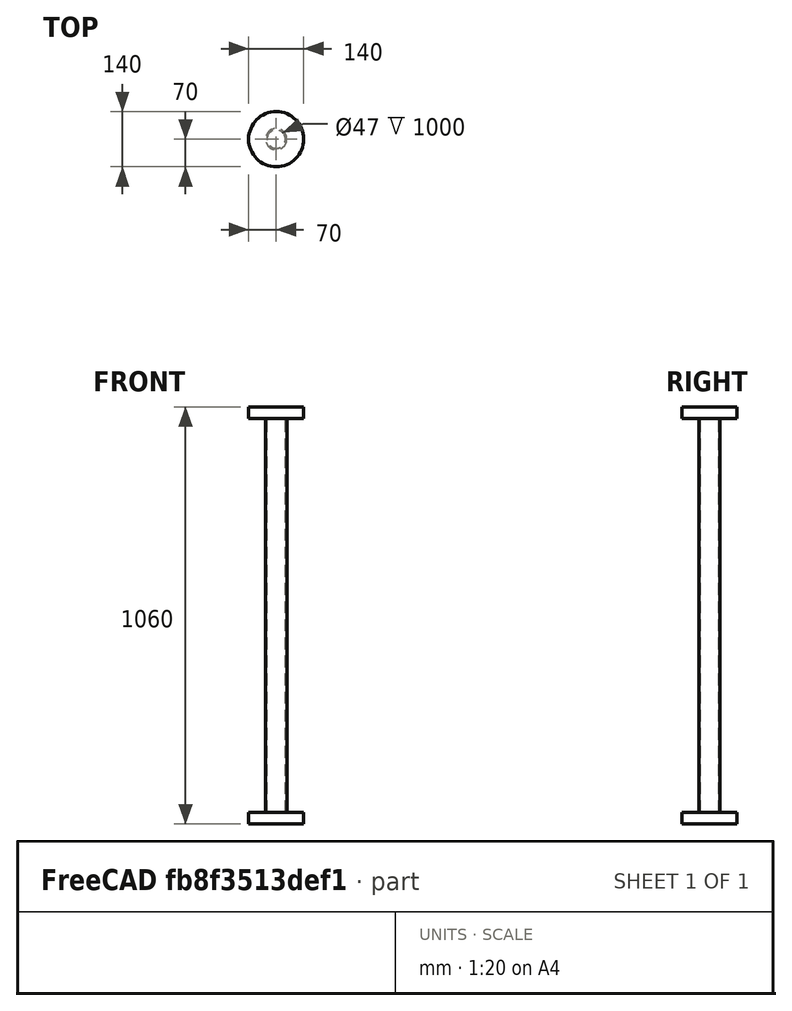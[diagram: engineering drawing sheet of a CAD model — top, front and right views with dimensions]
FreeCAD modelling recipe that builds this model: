
FCSTD DOCUMENT  (FreeCAD 0.19R)
Label: model
License: All rights reserved
LicenseURL: http://en.wikipedia.org/wiki/All_rights_reserved
objects: Mesh::Feature×3, Part::Cylinder×2, Part::FeaturePython×1
note: 3 computed .brp shape members not serialized (recipe doc carries the construction recipe); baked Part::Feature solids carry a one-line shape summary decoded from their .brp

FEATURE [Part::FeaturePython] Tube  # WARN: FeaturePython — macro-defined, semantics opaque (R4)
  AttacherType = Attacher::AttachEngine3D
  Height = 1000
  InnerRadius = 23.5
  OuterRadius = 27
FEATURE [Part::Cylinder] Cylinder001
  Angle = 360
  AttacherType = Attacher::AttachEngine3D
  Height = 30
  Placement = pos=(0,0,-30) rot=(0,0,1;0rad)
  Radius = 70
FEATURE [Part::Cylinder] Cylinder003
  Angle = 360
  AttacherType = Attacher::AttachEngine3D
  Height = 30
  Placement = pos=(0,0,1000) rot=(0,0,1;0rad)
  Radius = 70
FEATURE [Mesh::Feature] Mesh001  label="Cylinder001 (Meshed)"
FEATURE [Mesh::Feature] Mesh002  label="Cylinder003 (Meshed)"
FEATURE [Mesh::Feature] Mesh  label="Tube (Meshed)"
